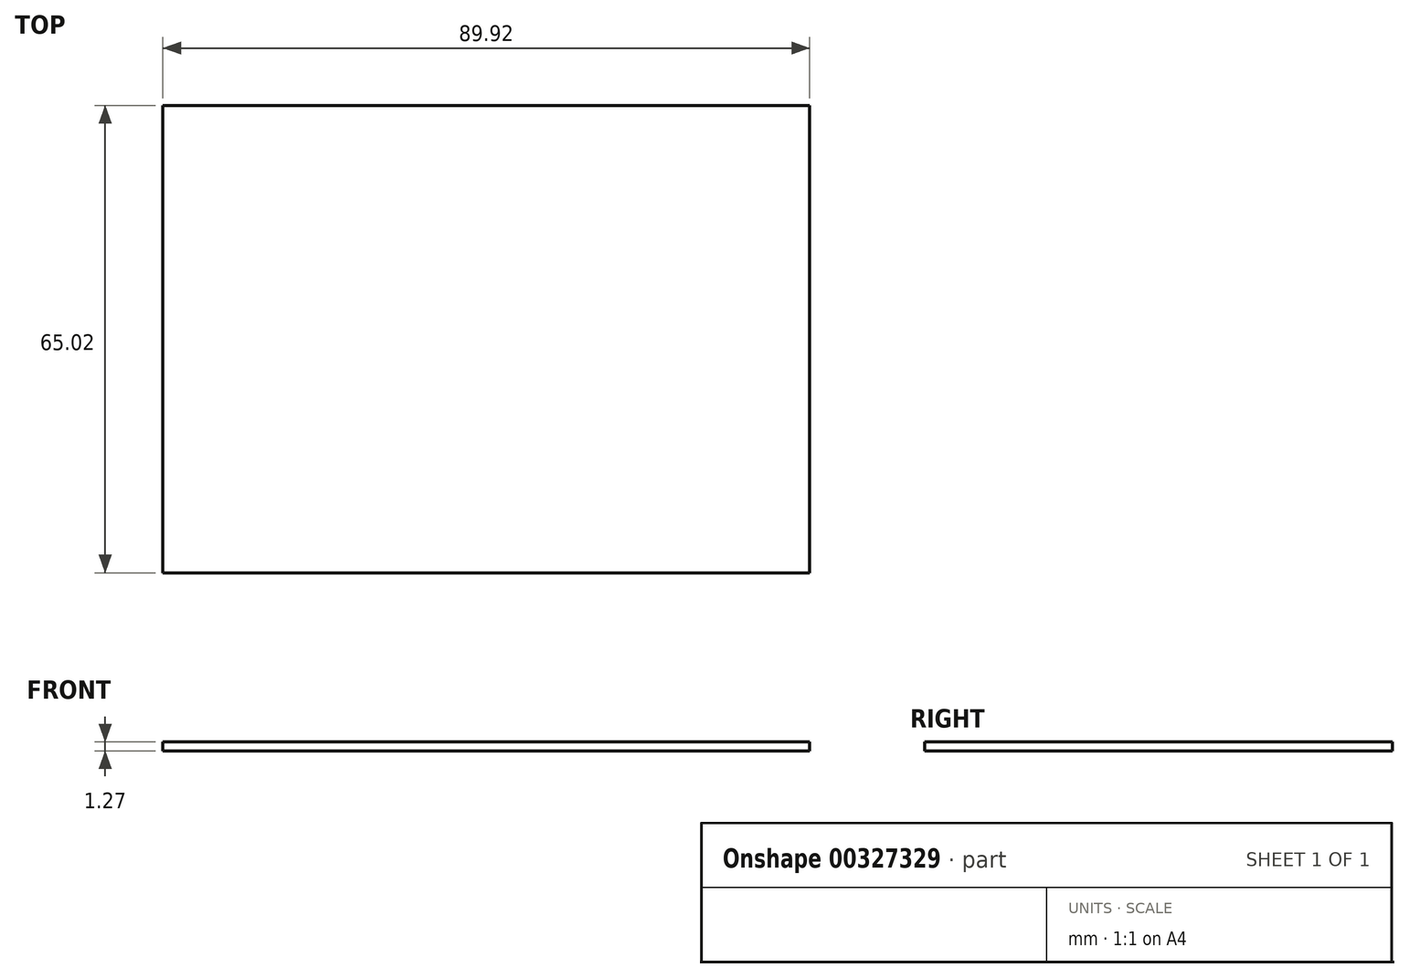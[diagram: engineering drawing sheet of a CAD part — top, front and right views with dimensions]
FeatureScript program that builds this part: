
annotation { "Feature Type Name" : "Feature", "Feature Type Description" : "" }
export const myFeature = defineFeature(function(context is Context, id is Id, definition is map)
    precondition{}
    {
        {
            var Q0;
            Q0=qCreatedBy(makeId("Top.planeOp"),FACE);
            var sketch = newSketch(context, id + "F0", { "sketchPlane" : qUnion([Q0])});
            skLineSegment(sketch, "E0.bottom", {"start": v(-44.96, 32.51) * mm, "end": v(44.96, 32.51) * mm});
            skLineSegment(sketch, "E0.top", {"start": v(-44.96, -32.51) * mm, "end": v(44.96, -32.51) * mm});
            skLineSegment(sketch, "E0.left", {"start": v(-44.96, 32.51) * mm, "end": v(-44.96, -32.51) * mm});
            skLineSegment(sketch, "E0.right", {"start": v(44.96, 32.51) * mm, "end": v(44.96, -32.51) * mm});
            skPoint(sketch, "E0.middle", {"position": v(0, 0) * mm});
            skSolve(sketch);
        }
        {
            var Q0;
            Q0 = qSketchRegion(id + "F0", true);
            extrude(context, id + "F1", {"entities" : qUnion([Q0]), "depth" : 1.27 * mm});
        }
    });
